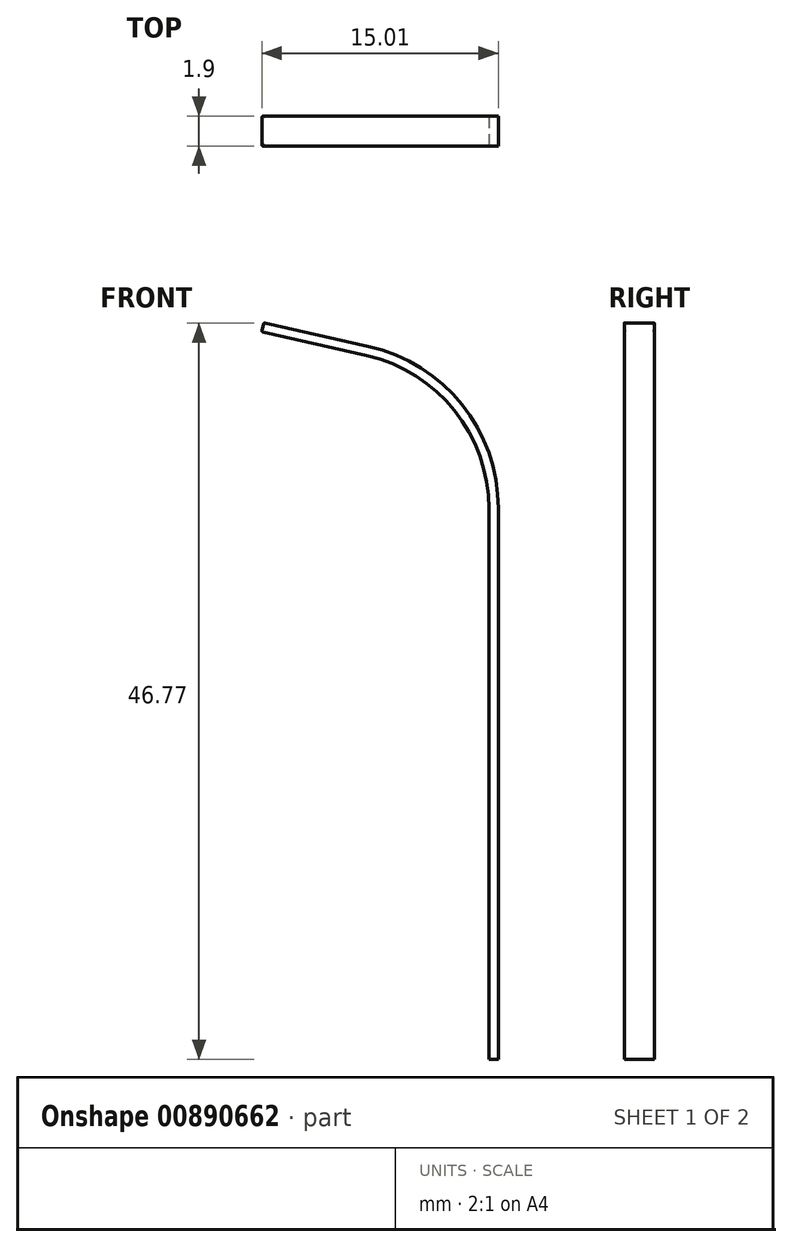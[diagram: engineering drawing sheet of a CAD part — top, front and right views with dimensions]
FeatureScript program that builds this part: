
annotation { "Feature Type Name" : "Feature", "Feature Type Description" : "" }
export const myFeature = defineFeature(function(context is Context, id is Id, definition is map)
    precondition{}
    {
        {
            var Q0;
            Q0=qCreatedBy(makeId("Front.planeOp"),FACE);
            var sketch = newSketch(context, id + "F0", { "sketchPlane" : qUnion([Q0])});
            skLineSegment(sketch, "E0", {"start": v(0, 0) * mm, "end": v(0, 35) * mm});
            skArc(sketch, "E1", {"start": v(0, 35) * mm, "mid": v(-2.25, 41.4) * mm, "end": v(-8, 45) * mm});
            skLineSegment(sketch, "E2", {"start": v(-8, 45) * mm, "end": v(-14.67, 46.5) * mm});
            skSolve(sketch);
        }
        {
            var Q0;
            Q0=qCreatedBy(makeId("Top.planeOp"),FACE);
            var sketch = newSketch(context, id + "F1", { "sketchPlane" : qUnion([Q0])});
            skLineSegment(sketch, "E3.bottom", {"start": v(-0.3, 0.95) * mm, "end": v(0.3, 0.95) * mm});
            skLineSegment(sketch, "E3.top", {"start": v(-0.3, -0.95) * mm, "end": v(0.3, -0.95) * mm});
            skLineSegment(sketch, "E3.left", {"start": v(-0.3, 0.95) * mm, "end": v(-0.3, -0.95) * mm});
            skLineSegment(sketch, "E3.right", {"start": v(0.3, 0.95) * mm, "end": v(0.3, -0.95) * mm});
            skSolve(sketch);
        }
        {
            var Q0;
            Q0=makeQuery(id+"F1.imprint","IMPRINT",FACE,{"disambiguationData":[TD([[makeQuery(id+"F1.imprint","IMPRINT",EDGE,{"derivedFrom":sQuery(id+"F1.wireOp",EDGE,"E3.bottom")}),-1.0]])]});
            var Q1;
            Q1=sQuery(id+"F0.wireOp",EDGE,"E0");
            var Q2;
            Q2=sQuery(id+"F0.wireOp",EDGE,"E1");
            var Q3;
            Q3=sQuery(id+"F0.wireOp",EDGE,"E2");
            sweep(context, id + "F2", {"profiles" : qUnion([Q0]), "path" : qUnion([Q1, Q2, Q3])});
        }
        {
            var Q0;
            Q0=makeQuery(id+"F2.opSweep","CAP_EDGE",EDGE,{"disambiguationData":[OSD([sQuery(id+"F0.wireOp",VERTEX,"E2.end"),sQuery(id+"F1.wireOp",EDGE,"E3.right")])],"isStart":false});
            var Q1;
            Q1=makeQuery(id+"F2.opSweep","CAP_EDGE",EDGE,{"disambiguationData":[OSD([sQuery(id+"F0.wireOp",VERTEX,"E2.end"),sQuery(id+"F1.wireOp",EDGE,"E3.left")])],"isStart":false});
            var Q2;
            Q2=makeQuery(id+"F2.opSweep","CAP_EDGE",EDGE,{"disambiguationData":[OSD([sQuery(id+"F0.wireOp",VERTEX,"E2.end"),sQuery(id+"F1.wireOp",EDGE,"E3.top")])],"isStart":false});
            var Q3;
            Q3=makeQuery(id+"F2.opSweep","CAP_EDGE",EDGE,{"disambiguationData":[OSD([sQuery(id+"F0.wireOp",VERTEX,"E2.end"),sQuery(id+"F1.wireOp",EDGE,"E3.bottom")])],"isStart":false});
            fillet(context, id + "F3", {"entities" : qUnion([Q0, Q1, Q2, Q3]), "radius" : 0.1 * mm, "tangentPropagation" : true, "allowEdgeOverflow" : false});
        }
    });
